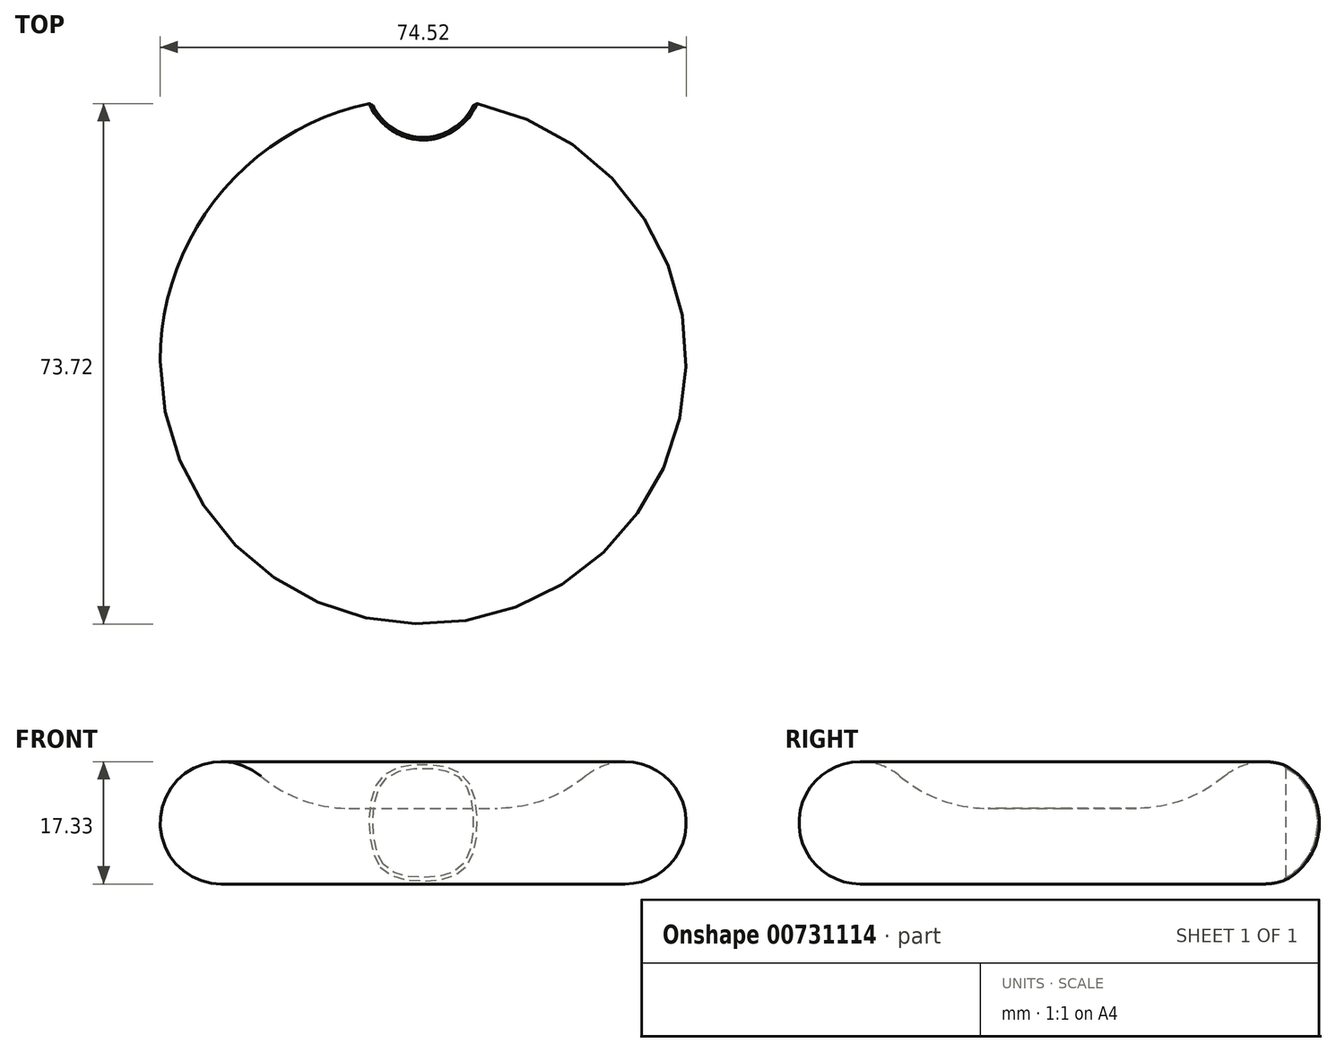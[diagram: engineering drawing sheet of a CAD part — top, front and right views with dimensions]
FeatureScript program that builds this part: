
annotation { "Feature Type Name" : "Feature", "Feature Type Description" : "" }
export const myFeature = defineFeature(function(context is Context, id is Id, definition is map)
    precondition{}
    {
        {
            var Q0;
            Q0=qCreatedBy(makeId("Front.planeOp"),FACE);
            var sketch = newSketch(context, id + "F0", { "sketchPlane" : qUnion([Q0])});
            skArc(sketch, "E0", {"start": v(-23, 15.29) * mm, "mid": v(-36.73, 11.64) * mm, "end": v(-28.6, 0) * mm});
            skArc(sketch, "E1", {"start": v(-23, 15.29) * mm, "mid": v(-17.16, 11.9) * mm, "end": v(-10.51, 10.72) * mm});
            skLineSegment(sketch, "E2", {"start": v(0, 0) * mm, "end": v(-28.6, 0) * mm});
            skLineSegment(sketch, "E3", {"start": v(0, 0) * mm, "end": v(0, 10.72) * mm});
            skLineSegment(sketch, "E4", {"start": v(0, 10.72) * mm, "end": v(-10.51, 10.72) * mm});
            skSolve(sketch);
        }
        {
            var Q0;
            Q0=makeQuery(id+"F0.imprint","IMPRINT",FACE,{"disambiguationData":[TD([[makeQuery(id+"F0.imprint","IMPRINT",EDGE,{"derivedFrom":sQuery(id+"F0.wireOp",EDGE,"E0")}),1.0]])]});
            var Q1;
            Q1=sQuery(id+"F0.wireOp",EDGE,"E3");
            revolve(context, id + "F1", {"surfaceOperationType" : NewSurfaceOperationType.NEW, "entities" : qUnion([Q0]), "axis" : qUnion([Q1]), "revolveType" : RevolveType.FULL});
        }
        {
            var Q0;
            Q0=qCreatedBy(makeId("Front.planeOp"),FACE);
            var sketch = newSketch(context, id + "F2", { "sketchPlane" : qUnion([Q0])});
            skCircle(sketch, "E5", {"center": v(-28.6, 8.67) * mm, "radius": 6.13 * mm});
            skSolve(sketch);
        }
        {
            var Q0;
            Q0=sQuery(id+"F2.wireOp",EDGE,"E5");
            var Q1;
            Q1=sQuery(id+"F0.wireOp",EDGE,"E3");
            revolve(context, id + "F3", {"bodyType" : ToolBodyType.SURFACE, "surfaceOperationType" : NewSurfaceOperationType.NEW, "surfaceEntities" : qUnion([Q0]), "axis" : qUnion([Q1]), "revolveType" : RevolveType.FULL});
        }
        {
            var Q0;
            Q0=qCreatedBy(makeId("Top.planeOp"),FACE);
            var sketch = newSketch(context, id + "F4", { "sketchPlane" : qUnion([Q0])});
            skCircle(sketch, "E6", {"center": v(0, 39.48) * mm, "radius": 7.83 * mm});
            skSolve(sketch);
        }
        {
            var Q0;
            Q0=makeQuery(id+"F4.imprint","IMPRINT",FACE,{"disambiguationData":[TD([[makeQuery(id+"F4.imprint","IMPRINT",EDGE,{"derivedFrom":sQuery(id+"F4.wireOp",EDGE,"E6")}),1.0]])]});
            var Q1;
            Q1 = qSketchRegion(id + "F4", true);
            extrude(context, id + "F5", {"entities" : qUnion([Q0, Q1]), "operationType" : NewBodyOperationType.REMOVE, "depth" : 25.4 * mm, "offsetDistance" : 25.4 * mm});
        }
        {
            var Q0;
            Q0=makeQuery(id+"F5.boolean.opBoolean","INTERSECT",EDGE,{"derivedFrom":[makeQuery(id+"F1.opRevolve","SWEPT_FACE",FACE,{"disambiguationData":[OSD([sQuery(id+"F0.wireOp",EDGE,"E0")])]}),makeQuery(id+"F5.opExtrude","SWEPT_FACE",FACE,{"disambiguationData":[OSD([sQuery(id+"F4.wireOp",EDGE,"E6")])]})]});
            chamfer(context, id + "F6", {"entities" : qUnion([Q0]), "width" : 0.5 * mm, "tangentPropagation" : true});
        }
    });
